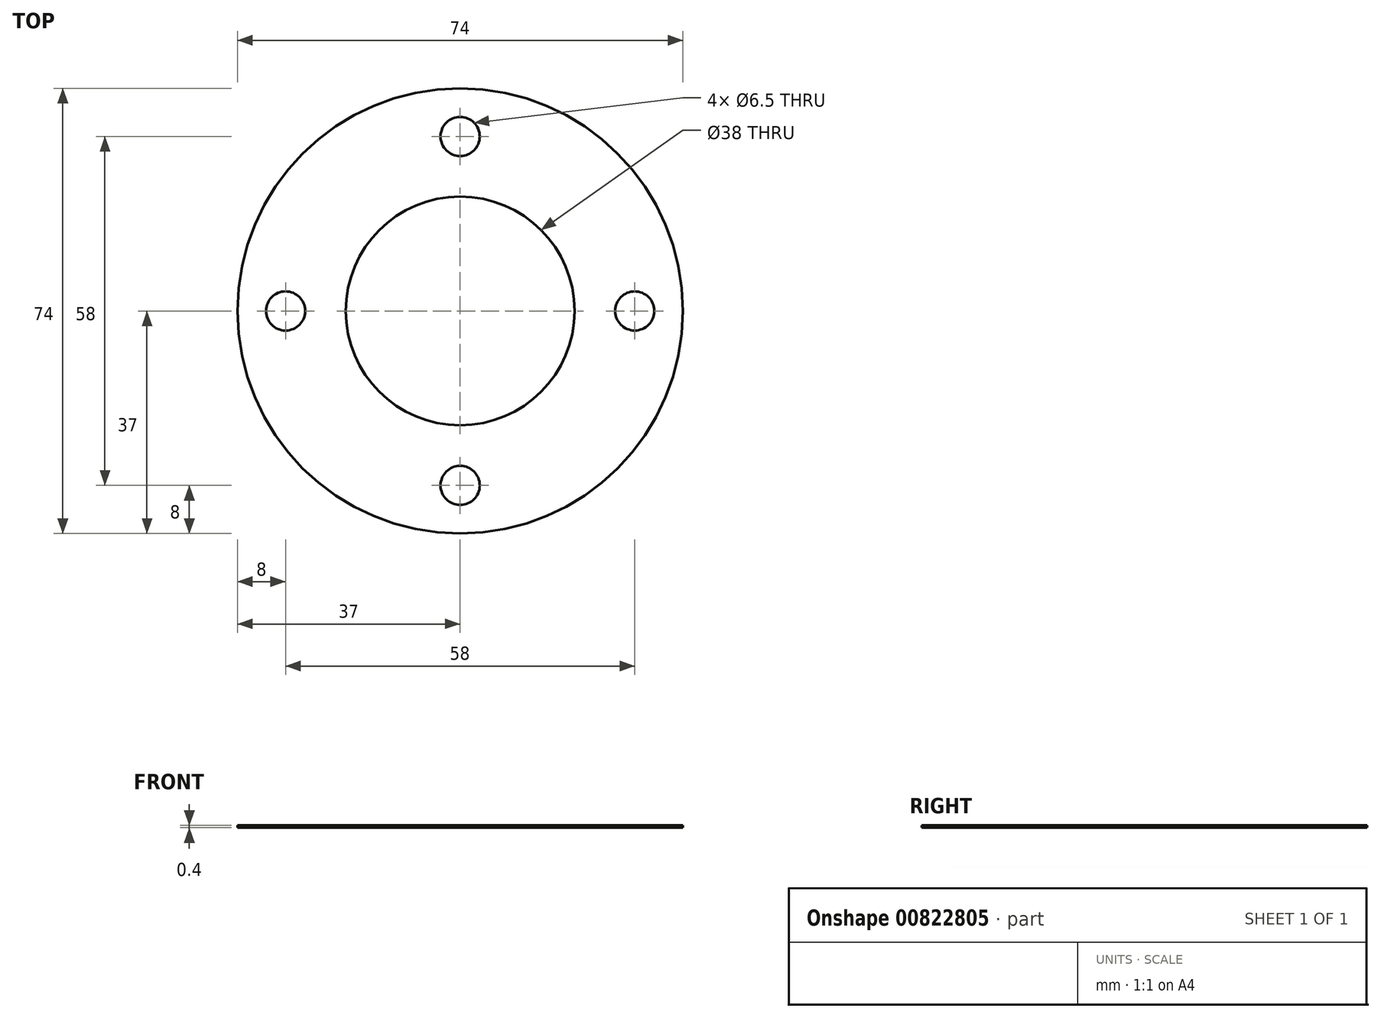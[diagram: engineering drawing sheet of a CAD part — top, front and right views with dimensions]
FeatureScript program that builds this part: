
annotation { "Feature Type Name" : "Feature", "Feature Type Description" : "" }
export const myFeature = defineFeature(function(context is Context, id is Id, definition is map)
    precondition{}
    {
        {
            var Q0;
            Q0=qCreatedBy(makeId("Top.planeOp"),FACE);
            var sketch = newSketch(context, id + "F0", { "sketchPlane" : qUnion([Q0])});
            skCircle(sketch, "E0", {"center": v(0, 0) * mm, "radius": 19 * mm});
            skCircle(sketch, "E1", {"center": v(0, 0) * mm, "radius": 29 * mm, "construction": true});
            skCircle(sketch, "E2", {"center": v(0, 0) * mm, "radius": 37 * mm});
            skLineSegment(sketch, "E3", {"start": v(0, -37) * mm, "end": v(0, 37) * mm, "construction": true});
            skLineSegment(sketch, "E4", {"start": v(0, 37) * mm, "end": v(37, 0) * mm, "construction": true});
            skLineSegment(sketch, "E5", {"start": v(37, 0) * mm, "end": v(-37, 0) * mm, "construction": true});
            skCircle(sketch, "E6", {"center": v(0, 29) * mm, "radius": 3.25 * mm});
            skCircle(sketch, "E7", {"center": v(-29, 0) * mm, "radius": 3.25 * mm});
            skCircle(sketch, "E8", {"center": v(0, -29) * mm, "radius": 3.25 * mm});
            skCircle(sketch, "E9", {"center": v(29, 0) * mm, "radius": 3.25 * mm});
            skSolve(sketch);
        }
        {
            var Q0;
            Q0=qSketchRegion(id+"F0",true);
            extrude(context, id + "F1", {"entities" : qUnion([Q0]), "depth" : 0.4 * mm, "offsetDistance" : 25 * mm});
        }
    });
